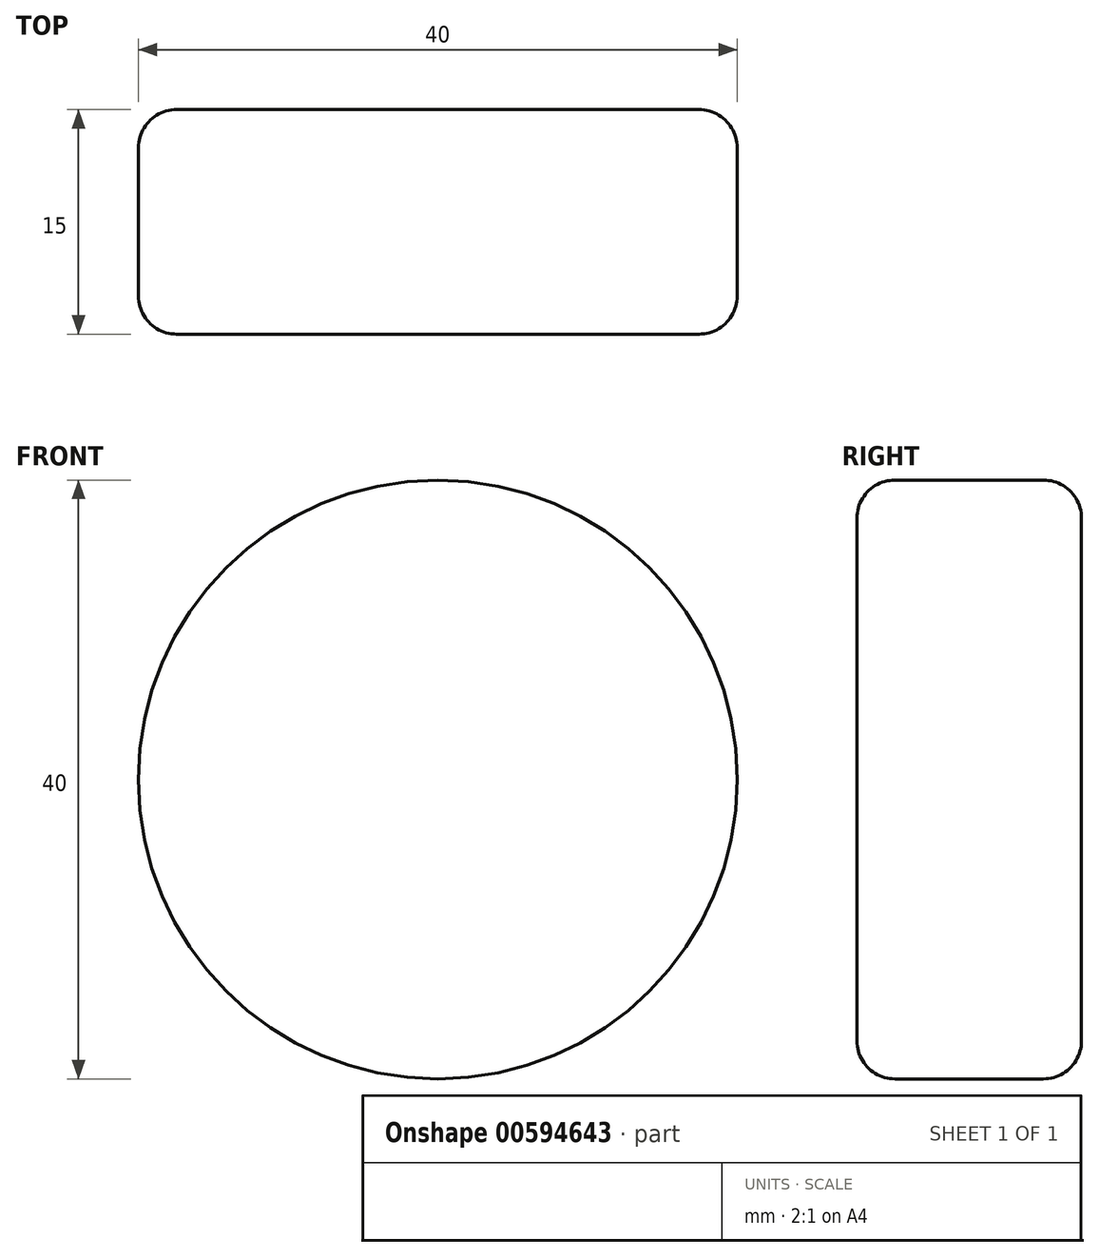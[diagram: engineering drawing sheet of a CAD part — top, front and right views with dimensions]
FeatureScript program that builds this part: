
annotation { "Feature Type Name" : "Feature", "Feature Type Description" : "" }
export const myFeature = defineFeature(function(context is Context, id is Id, definition is map)
    precondition{}
    {
        {
            var Q0;
            Q0=qCreatedBy(makeId("Front.planeOp"),FACE);
            var sketch = newSketch(context, id + "F0", { "sketchPlane" : qUnion([Q0])});
            skCircle(sketch, "E0", {"center": v(0, 0) * mm, "radius": 17.5 * mm, "construction": true});
            skCircle(sketch, "E1", {"center": v(0, 0) * mm, "radius": 20 * mm});
            skSolve(sketch);
        }
        {
            var Q0;
            Q0 = qSketchRegion(id + "F0", true);
            extrude(context, id + "F1", {"entities" : qUnion([Q0]), "depth" : 15 * mm, "offsetDistance" : 25.4 * mm});
        }
        {
            var Q0;
            Q0=makeQuery(id+"F1.opExtrude","CAP_EDGE",EDGE,{"disambiguationData":[OSD([sQuery(id+"F0.wireOp",EDGE,"E1")])],"isStart":true});
            var Q1;
            Q1=makeQuery(id+"F1.opExtrude","CAP_EDGE",EDGE,{"disambiguationData":[OSD([sQuery(id+"F0.wireOp",EDGE,"E1")])],"isStart":false});
            fillet(context, id + "F2", {"entities" : qUnion([Q0, Q1]), "radius" : 2.54 * mm, "tangentPropagation" : true, "allowEdgeOverflow" : false});
        }
    });
